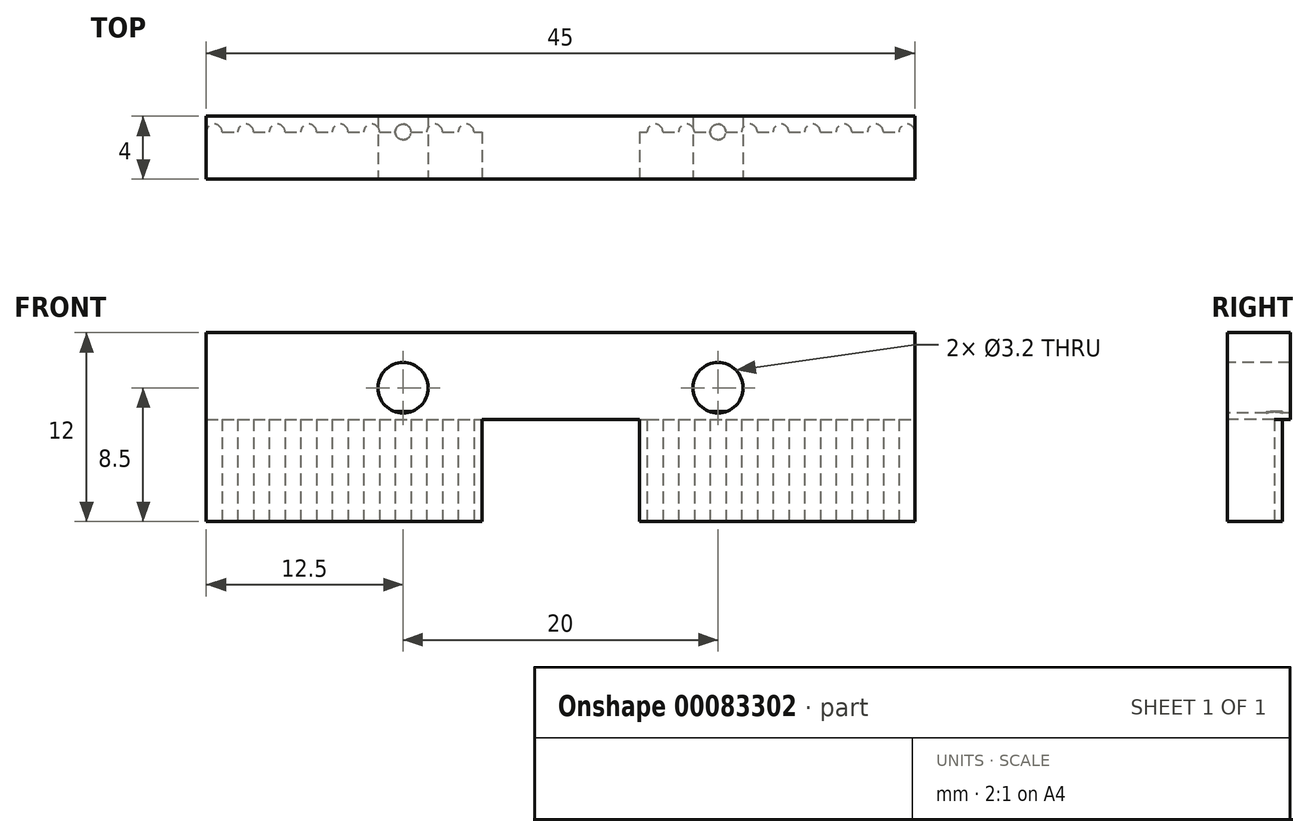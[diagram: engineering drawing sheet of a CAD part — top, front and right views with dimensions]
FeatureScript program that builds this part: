
annotation { "Feature Type Name" : "Feature", "Feature Type Description" : "" }
export const myFeature = defineFeature(function(context is Context, id is Id, definition is map)
    precondition{}
    {
        {
            var Q0;
            Q0=qCreatedBy(makeId("Top.planeOp"),FACE);
            var sketch = newSketch(context, id + "F0", { "sketchPlane" : qUnion([Q0])});
            skLineSegment(sketch, "E0.bottom", {"start": v(22.5, 2) * mm, "end": v(-22.5, 2) * mm});
            skLineSegment(sketch, "E0.top", {"start": v(22.5, -2) * mm, "end": v(-22.5, -2) * mm});
            skLineSegment(sketch, "E0.left", {"start": v(22.5, 2) * mm, "end": v(22.5, -2) * mm});
            skLineSegment(sketch, "E0.right", {"start": v(-22.5, 2) * mm, "end": v(-22.5, -2) * mm});
            skPoint(sketch, "E0.middle", {"position": v(0, 0) * mm});
            skSolve(sketch);
        }
        {
            var Q0;
            Q0 = qSketchRegion(id + "F0", true);
            extrude(context, id + "F1", {"entities" : qUnion([Q0]), "depth" : 12 * mm});
        }
        {
            var Q0;
            Q0=makeQuery(id+"F1.opExtrude","SWEPT_FACE",FACE,{"disambiguationData":[OSD([sQuery(id+"F0.wireOp",EDGE,"E0.top")])]});
            var sketch = newSketch(context, id + "F2", { "sketchPlane" : qUnion([Q0])});
            skCircle(sketch, "E1", {"center": v(-10, 8.5) * mm, "radius": 1.6 * mm});
            skCircle(sketch, "E2", {"center": v(10, 8.5) * mm, "radius": 1.6 * mm});
            skSolve(sketch);
        }
        {
            var Q0;
            Q0 = qSketchRegion(id + "F2", true);
            extrude(context, id + "F3", {"entities" : qUnion([Q0]), "operationType" : NewBodyOperationType.REMOVE, "endBound" : BoundingType.THROUGH_ALL, "oppositeDirection" : true, "depth" : 25 * mm});
        }
        {
            var Q0;
            Q0=makeQuery(id+"F1.opExtrude","CAP_FACE",FACE,{"disambiguationData":[OSD([sQuery(id+"F0.wireOp",EDGE,"E0.bottom"),sQuery(id+"F0.wireOp",EDGE,"E0.top"),sQuery(id+"F0.wireOp",EDGE,"E0.left"),sQuery(id+"F0.wireOp",EDGE,"E0.right")])],"isStart":true});
            var sketch = newSketch(context, id + "F4", { "sketchPlane" : qUnion([Q0])});
            skLineSegment(sketch, "E3.bottom", {"start": v(-22.5, -2) * mm, "end": v(22.5, -2) * mm});
            skLineSegment(sketch, "E3.top", {"start": v(-22.5, -1) * mm, "end": v(22.5, -1) * mm});
            skLineSegment(sketch, "E3.left", {"start": v(-22.5, -2) * mm, "end": v(-22.5, -1) * mm});
            skLineSegment(sketch, "E3.right", {"start": v(22.5, -2) * mm, "end": v(22.5, -1) * mm});
            skSolve(sketch);
        }
        {
            var Q0;
            Q0 = qSketchRegion(id + "F4", true);
            extrude(context, id + "F5", {"entities" : qUnion([Q0]), "operationType" : NewBodyOperationType.REMOVE, "oppositeDirection" : true, "depth" : 6.5 * mm});
        }
        {
            var Q0;
            Q0=makeQuery(id+"F1.opExtrude","CAP_FACE",FACE,{"disambiguationData":[OSD([sQuery(id+"F0.wireOp",EDGE,"E0.bottom"),sQuery(id+"F0.wireOp",EDGE,"E0.top"),sQuery(id+"F0.wireOp",EDGE,"E0.left"),sQuery(id+"F0.wireOp",EDGE,"E0.right")])],"isStart":true});
            var sketch = newSketch(context, id + "F6", { "sketchPlane" : qUnion([Q0])});
            skCircle(sketch, "E4", {"center": v(22, -1) * mm, "radius": 0.5 * mm});
            skCircle(sketch, "E5.1.0.0", {"center": v(20, -1) * mm, "radius": 0.5 * mm});
            skCircle(sketch, "E5.2.0.0", {"center": v(18, -1) * mm, "radius": 0.5 * mm});
            skCircle(sketch, "E5.3.0.0", {"center": v(16, -1) * mm, "radius": 0.5 * mm});
            skCircle(sketch, "E5.4.0.0", {"center": v(14, -1) * mm, "radius": 0.5 * mm});
            skCircle(sketch, "E5.5.0.0", {"center": v(12, -1) * mm, "radius": 0.5 * mm});
            skCircle(sketch, "E5.6.0.0", {"center": v(10, -1) * mm, "radius": 0.5 * mm});
            skCircle(sketch, "E5.7.0.0", {"center": v(8, -1) * mm, "radius": 0.5 * mm});
            skCircle(sketch, "E5.8.0.0", {"center": v(6, -1) * mm, "radius": 0.5 * mm});
            skCircle(sketch, "E5.9.0.0", {"center": v(4, -1) * mm, "radius": 0.5 * mm});
            skCircle(sketch, "E5.10.0.0", {"center": v(2, -1) * mm, "radius": 0.5 * mm});
            skCircle(sketch, "E5.11.0.0", {"center": v(0, -1) * mm, "radius": 0.5 * mm});
            skCircle(sketch, "E5.12.0.0", {"center": v(-2, -1) * mm, "radius": 0.5 * mm});
            skCircle(sketch, "E5.13.0.0", {"center": v(-4, -1) * mm, "radius": 0.5 * mm});
            skCircle(sketch, "E5.14.0.0", {"center": v(-6, -1) * mm, "radius": 0.5 * mm});
            skCircle(sketch, "E5.15.0.0", {"center": v(-8, -1) * mm, "radius": 0.5 * mm});
            skCircle(sketch, "E5.16.0.0", {"center": v(-10, -1) * mm, "radius": 0.5 * mm});
            skCircle(sketch, "E5.17.0.0", {"center": v(-12, -1) * mm, "radius": 0.5 * mm});
            skCircle(sketch, "E5.18.0.0", {"center": v(-14, -1) * mm, "radius": 0.5 * mm});
            skCircle(sketch, "E5.19.0.0", {"center": v(-16, -1) * mm, "radius": 0.5 * mm});
            skCircle(sketch, "E5.20.0.0", {"center": v(-18, -1) * mm, "radius": 0.5 * mm});
            skCircle(sketch, "E5.21.0.0", {"center": v(-20, -1) * mm, "radius": 0.5 * mm});
            skCircle(sketch, "E5.22.0.0", {"center": v(-22, -1) * mm, "radius": 0.5 * mm});
            skLineSegment(sketch, "E5.direction1", {"start": v(22, -1) * mm, "end": v(20, -1) * mm, "construction": true});
            skSolve(sketch);
        }
        {
            var Q0;
            Q0 = qSketchRegion(id + "F6", true);
            extrude(context, id + "F7", {"entities" : qUnion([Q0]), "operationType" : NewBodyOperationType.ADD, "oppositeDirection" : true, "depth" : 7 * mm});
        }
        {
            var Q0;
            Q0=makeQuery(id+"F7.boolean.opBoolean","MERGE",FACE,{"derivedFrom":[makeQuery(id+"F1.opExtrude","CAP_FACE",FACE,{"disambiguationData":[OSD([sQuery(id+"F0.wireOp",EDGE,"E0.bottom"),sQuery(id+"F0.wireOp",EDGE,"E0.top"),sQuery(id+"F0.wireOp",EDGE,"E0.left"),sQuery(id+"F0.wireOp",EDGE,"E0.right")])],"isStart":true}),makeQuery(id+"F7.opExtrude","CAP_FACE",FACE,{"disambiguationData":[OSD([sQuery(id+"F6.wireOp",EDGE,"E4")])],"isStart":true}),makeQuery(id+"F7.opExtrude","CAP_FACE",FACE,{"disambiguationData":[OSD([sQuery(id+"F6.wireOp",EDGE,"E5.1.0.0")])],"isStart":true}),makeQuery(id+"F7.opExtrude","CAP_FACE",FACE,{"disambiguationData":[OSD([sQuery(id+"F6.wireOp",EDGE,"E5.2.0.0")])],"isStart":true}),makeQuery(id+"F7.opExtrude","CAP_FACE",FACE,{"disambiguationData":[OSD([sQuery(id+"F6.wireOp",EDGE,"E5.3.0.0")])],"isStart":true}),makeQuery(id+"F7.opExtrude","CAP_FACE",FACE,{"disambiguationData":[OSD([sQuery(id+"F6.wireOp",EDGE,"E5.4.0.0")])],"isStart":true}),makeQuery(id+"F7.opExtrude","CAP_FACE",FACE,{"disambiguationData":[OSD([sQuery(id+"F6.wireOp",EDGE,"E5.5.0.0")])],"isStart":true}),makeQuery(id+"F7.opExtrude","CAP_FACE",FACE,{"disambiguationData":[OSD([sQuery(id+"F6.wireOp",EDGE,"E5.6.0.0")])],"isStart":true}),makeQuery(id+"F7.opExtrude","CAP_FACE",FACE,{"disambiguationData":[OSD([sQuery(id+"F6.wireOp",EDGE,"E5.7.0.0")])],"isStart":true}),makeQuery(id+"F7.opExtrude","CAP_FACE",FACE,{"disambiguationData":[OSD([sQuery(id+"F6.wireOp",EDGE,"E5.8.0.0")])],"isStart":true}),makeQuery(id+"F7.opExtrude","CAP_FACE",FACE,{"disambiguationData":[OSD([sQuery(id+"F6.wireOp",EDGE,"E5.9.0.0")])],"isStart":true}),makeQuery(id+"F7.opExtrude","CAP_FACE",FACE,{"disambiguationData":[OSD([sQuery(id+"F6.wireOp",EDGE,"E5.10.0.0")])],"isStart":true}),makeQuery(id+"F7.opExtrude","CAP_FACE",FACE,{"disambiguationData":[OSD([sQuery(id+"F6.wireOp",EDGE,"E5.11.0.0")])],"isStart":true}),makeQuery(id+"F7.opExtrude","CAP_FACE",FACE,{"disambiguationData":[OSD([sQuery(id+"F6.wireOp",EDGE,"E5.12.0.0")])],"isStart":true}),makeQuery(id+"F7.opExtrude","CAP_FACE",FACE,{"disambiguationData":[OSD([sQuery(id+"F6.wireOp",EDGE,"E5.13.0.0")])],"isStart":true}),makeQuery(id+"F7.opExtrude","CAP_FACE",FACE,{"disambiguationData":[OSD([sQuery(id+"F6.wireOp",EDGE,"E5.14.0.0")])],"isStart":true}),makeQuery(id+"F7.opExtrude","CAP_FACE",FACE,{"disambiguationData":[OSD([sQuery(id+"F6.wireOp",EDGE,"E5.15.0.0")])],"isStart":true}),makeQuery(id+"F7.opExtrude","CAP_FACE",FACE,{"disambiguationData":[OSD([sQuery(id+"F6.wireOp",EDGE,"E5.16.0.0")])],"isStart":true}),makeQuery(id+"F7.opExtrude","CAP_FACE",FACE,{"disambiguationData":[OSD([sQuery(id+"F6.wireOp",EDGE,"E5.17.0.0")])],"isStart":true}),makeQuery(id+"F7.opExtrude","CAP_FACE",FACE,{"disambiguationData":[OSD([sQuery(id+"F6.wireOp",EDGE,"E5.18.0.0")])],"isStart":true}),makeQuery(id+"F7.opExtrude","CAP_FACE",FACE,{"disambiguationData":[OSD([sQuery(id+"F6.wireOp",EDGE,"E5.19.0.0")])],"isStart":true}),makeQuery(id+"F7.opExtrude","CAP_FACE",FACE,{"disambiguationData":[OSD([sQuery(id+"F6.wireOp",EDGE,"E5.20.0.0")])],"isStart":true}),makeQuery(id+"F7.opExtrude","CAP_FACE",FACE,{"disambiguationData":[OSD([sQuery(id+"F6.wireOp",EDGE,"E5.21.0.0")])],"isStart":true}),makeQuery(id+"F7.opExtrude","CAP_FACE",FACE,{"disambiguationData":[OSD([sQuery(id+"F6.wireOp",EDGE,"E5.22.0.0")])],"isStart":true})]});
            var sketch = newSketch(context, id + "F8", { "sketchPlane" : qUnion([Q0])});
            skLineSegment(sketch, "E6.bottom", {"start": v(5, -4.87) * mm, "end": v(-5, -4.87) * mm});
            skLineSegment(sketch, "E6.top", {"start": v(5, 4.87) * mm, "end": v(-5, 4.87) * mm});
            skLineSegment(sketch, "E6.left", {"start": v(5, -4.87) * mm, "end": v(5, 4.87) * mm});
            skLineSegment(sketch, "E6.right", {"start": v(-5, -4.87) * mm, "end": v(-5, 4.87) * mm});
            skPoint(sketch, "E6.middle", {"position": v(0, 0) * mm});
            skSolve(sketch);
        }
        {
            var Q0;
            Q0 = qSketchRegion(id + "F8", true);
            extrude(context, id + "F9", {"entities" : qUnion([Q0]), "operationType" : NewBodyOperationType.REMOVE, "oppositeDirection" : true, "depth" : 6.5 * mm});
        }
    });
